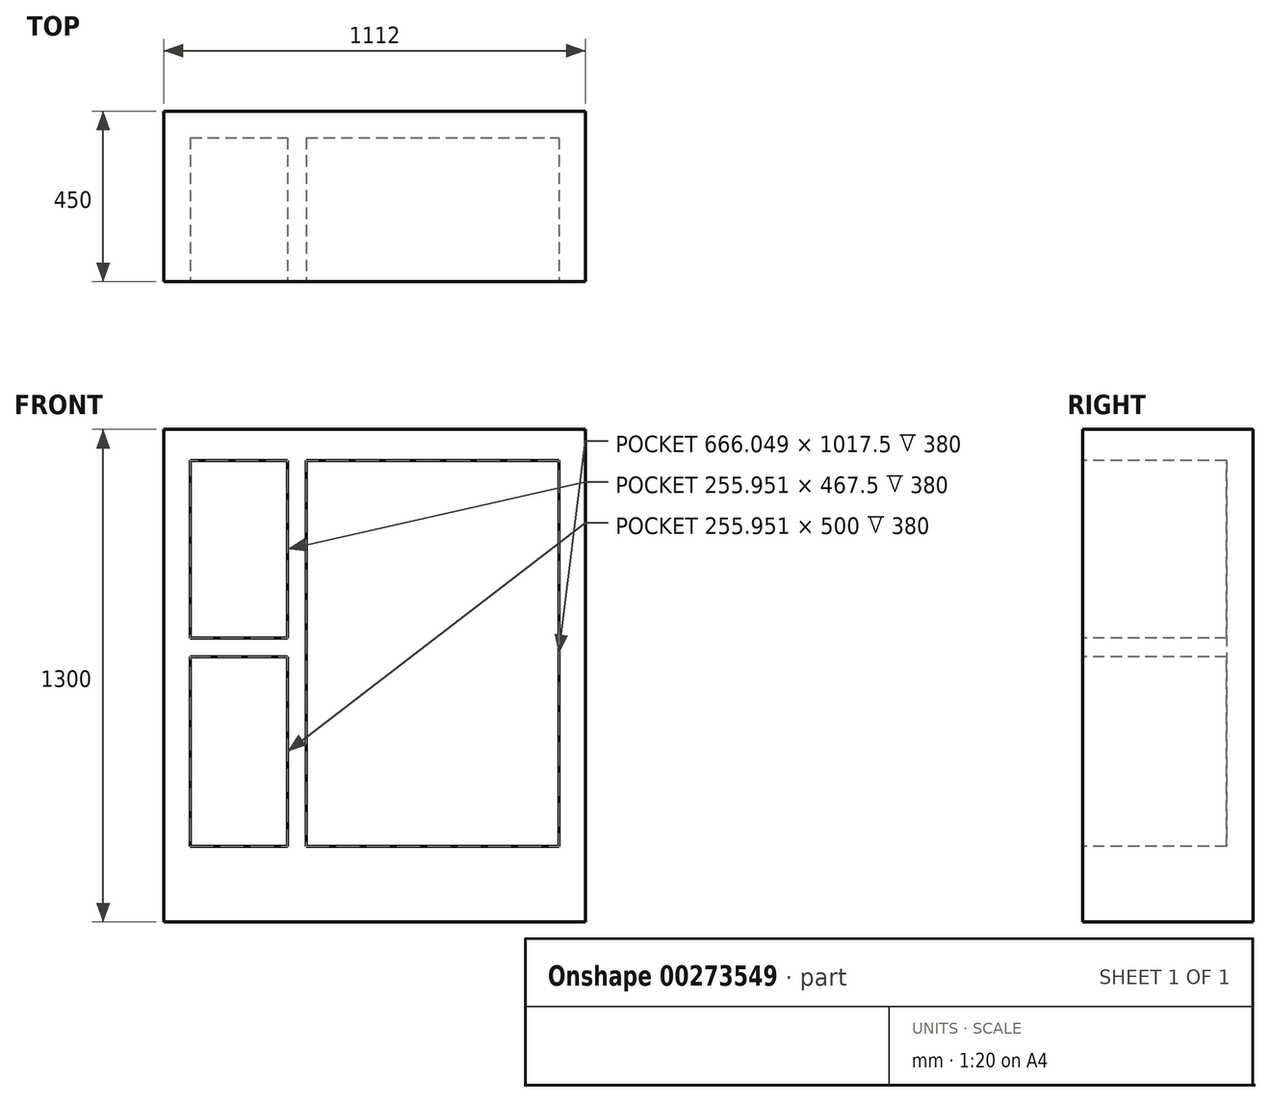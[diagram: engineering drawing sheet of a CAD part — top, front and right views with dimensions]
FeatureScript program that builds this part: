
annotation { "Feature Type Name" : "Feature", "Feature Type Description" : "" }
export const myFeature = defineFeature(function(context is Context, id is Id, definition is map)
    precondition{}
    {
        {
            var Q0;
            Q0=qCreatedBy(makeId("Top.planeOp"),FACE);
            var sketch = newSketch(context, id + "F0", { "sketchPlane" : qUnion([Q0])});
            skLineSegment(sketch, "E0.bottom", {"start": v(-556, -225) * mm, "end": v(556, -225) * mm});
            skLineSegment(sketch, "E0.top", {"start": v(-556, 225) * mm, "end": v(556, 225) * mm});
            skLineSegment(sketch, "E0.left", {"start": v(-556, -225) * mm, "end": v(-556, 225) * mm});
            skLineSegment(sketch, "E0.right", {"start": v(556, -225) * mm, "end": v(556, 225) * mm});
            skPoint(sketch, "E0.middle", {"position": v(0, 0) * mm});
            skSolve(sketch);
        }
        {
            var Q0;
            Q0 = qSketchRegion(id + "F0", true);
            extrude(context, id + "F1", {"entities" : qUnion([Q0]), "oppositeDirection" : true, "depth" : 1300 * mm});
        }
        {
            var Q0;
            Q0=makeQuery(id+"F1.opExtrude","SWEPT_FACE",FACE,{"disambiguationData":[OSD([sQuery(id+"F0.wireOp",EDGE,"E0.bottom")])]});
            var sketch = newSketch(context, id + "F2", { "sketchPlane" : qUnion([Q0])});
            skLineSegment(sketch, "E1.bottom", {"start": v(-486, -1100) * mm, "end": v(486, -1100) * mm});
            skLineSegment(sketch, "E1.top", {"start": v(-486, -82.5) * mm, "end": v(486, -82.5) * mm});
            skLineSegment(sketch, "E1.left", {"start": v(-486, -1100) * mm, "end": v(-486, -82.5) * mm});
            skLineSegment(sketch, "E1.right", {"start": v(486, -1100) * mm, "end": v(486, -82.5) * mm});
            skPoint(sketch, "E1.middle", {"position": v(0, -591.25) * mm});
            skSolve(sketch);
        }
        {
            var Q0;
            Q0=makeQuery(id+"F2.imprint","IMPRINT",FACE,{"disambiguationData":[TD([[makeQuery(id+"F2.imprint","IMPRINT",EDGE,{"derivedFrom":sQuery(id+"F2.wireOp",EDGE,"E1.bottom")}),1.0]])]});
            extrude(context, id + "F3", {"entities" : qUnion([Q0]), "operationType" : NewBodyOperationType.REMOVE, "oppositeDirection" : true, "depth" : 380 * mm});
        }
        {
            var Q0;
            Q0=makeQuery(id+"F1.opExtrude","SWEPT_FACE",FACE,{"disambiguationData":[OSD([sQuery(id+"F0.wireOp",EDGE,"E0.bottom")])]});
            var sketch = newSketch(context, id + "F4", { "sketchPlane" : qUnion([Q0])});
            skLineSegment(sketch, "E2.bottom", {"start": v(-230.05, -82.5) * mm, "end": v(-180.05, -82.5) * mm});
            skLineSegment(sketch, "E2.top", {"start": v(-230.05, -1100) * mm, "end": v(-180.05, -1100) * mm});
            skLineSegment(sketch, "E2.left", {"start": v(-230.05, -82.5) * mm, "end": v(-230.05, -1100) * mm});
            skLineSegment(sketch, "E2.right", {"start": v(-180.05, -82.5) * mm, "end": v(-180.05, -1100) * mm});
            skLineSegment(sketch, "E3.bottom", {"start": v(-486, -550) * mm, "end": v(-180.05, -550) * mm});
            skLineSegment(sketch, "E3.top", {"start": v(-486, -600) * mm, "end": v(-180.05, -600) * mm});
            skLineSegment(sketch, "E3.left", {"start": v(-486, -550) * mm, "end": v(-486, -600) * mm});
            skLineSegment(sketch, "E3.right", {"start": v(-180.05, -550) * mm, "end": v(-180.05, -600) * mm});
            skSolve(sketch);
        }
        {
            var Q0;
            Q0 = qSketchRegion(id + "F4", true);
            extrude(context, id + "F5", {"entities" : qUnion([Q0]), "operationType" : NewBodyOperationType.ADD, "oppositeDirection" : true, "depth" : 380 * mm});
        }
    });
